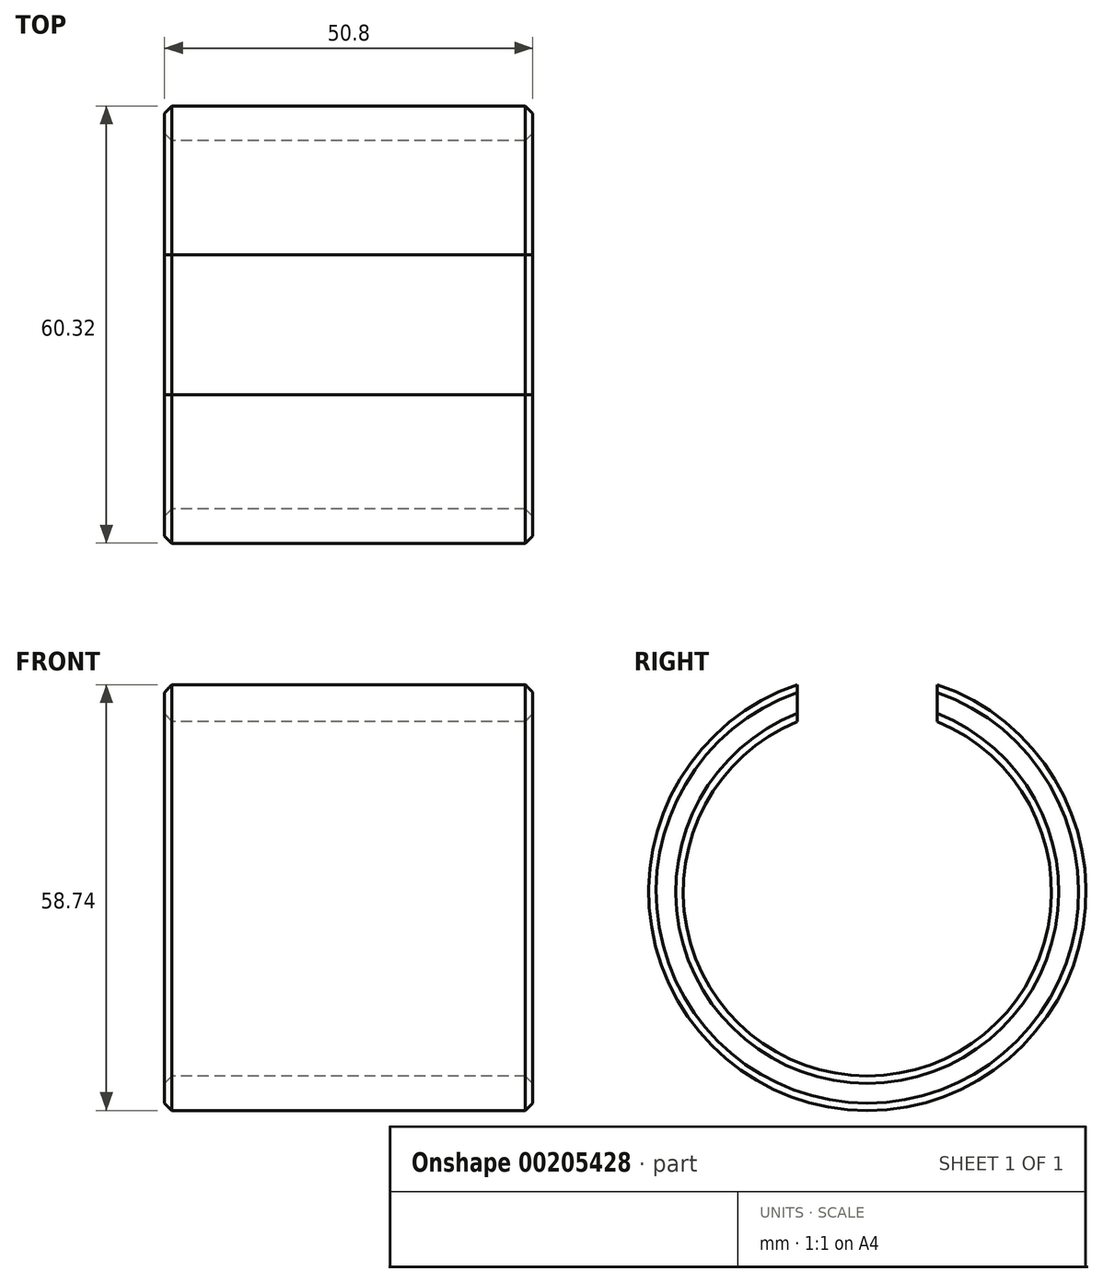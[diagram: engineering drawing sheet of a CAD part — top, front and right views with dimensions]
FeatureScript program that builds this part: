
annotation { "Feature Type Name" : "Feature", "Feature Type Description" : "" }
export const myFeature = defineFeature(function(context is Context, id is Id, definition is map)
    precondition{}
    {
        {
            var Q0;
            Q0=qCreatedBy(makeId("Right.planeOp"),FACE);
            var sketch = newSketch(context, id + "F0", { "sketchPlane" : qUnion([Q0])});
            skArc(sketch, "E0", {"start": v(-9.65, 28.58) * mm, "mid": v(0, -30.16) * mm, "end": v(9.65, 28.58) * mm});
            skArc(sketch, "E1", {"start": v(-9.65, 23.5) * mm, "mid": v(0, -25.4) * mm, "end": v(9.65, 23.5) * mm});
            skLineSegment(sketch, "E2", {"start": v(0, 0) * mm, "end": v(0, 44.25) * mm});
            skLineSegment(sketch, "E3.0", {"start": v(9.65, 0) * mm, "end": v(9.65, 44.25) * mm});
            skLineSegment(sketch, "E4.MirrorCS", {"start": v(-9.65, 0) * mm, "end": v(-9.65, 44.25) * mm});
            skSolve(sketch);
        }
        {
            var Q0;
            Q0 = qSketchRegion(id + "F0", true);
            extrude(context, id + "F1", {"entities" : qUnion([Q0]), "endBound" : BoundingType.SYMMETRIC, "depth" : 50.8 * mm});
        }
        {
            var Q0;
            Q0=makeQuery(id+"F1.opExtrude","CAP_EDGE",EDGE,{"disambiguationData":[OSD([sQuery(id+"F0.wireOp",EDGE,"E0")])],"isStart":false});
            var Q1;
            Q1=makeQuery(id+"F1.opExtrude","CAP_EDGE",EDGE,{"disambiguationData":[OSD([sQuery(id+"F0.wireOp",EDGE,"E1")])],"isStart":false});
            var Q2;
            Q2=makeQuery(id+"F1.opExtrude","CAP_EDGE",EDGE,{"disambiguationData":[OSD([sQuery(id+"F0.wireOp",EDGE,"E0")])],"isStart":true});
            var Q3;
            Q3=makeQuery(id+"F1.opExtrude","CAP_EDGE",EDGE,{"disambiguationData":[OSD([sQuery(id+"F0.wireOp",EDGE,"E1")])],"isStart":true});
            chamfer(context, id + "F2", {"entities" : qUnion([Q0, Q1, Q2, Q3]), "width" : 1.02 * mm, "tangentPropagation" : true});
        }
    });
